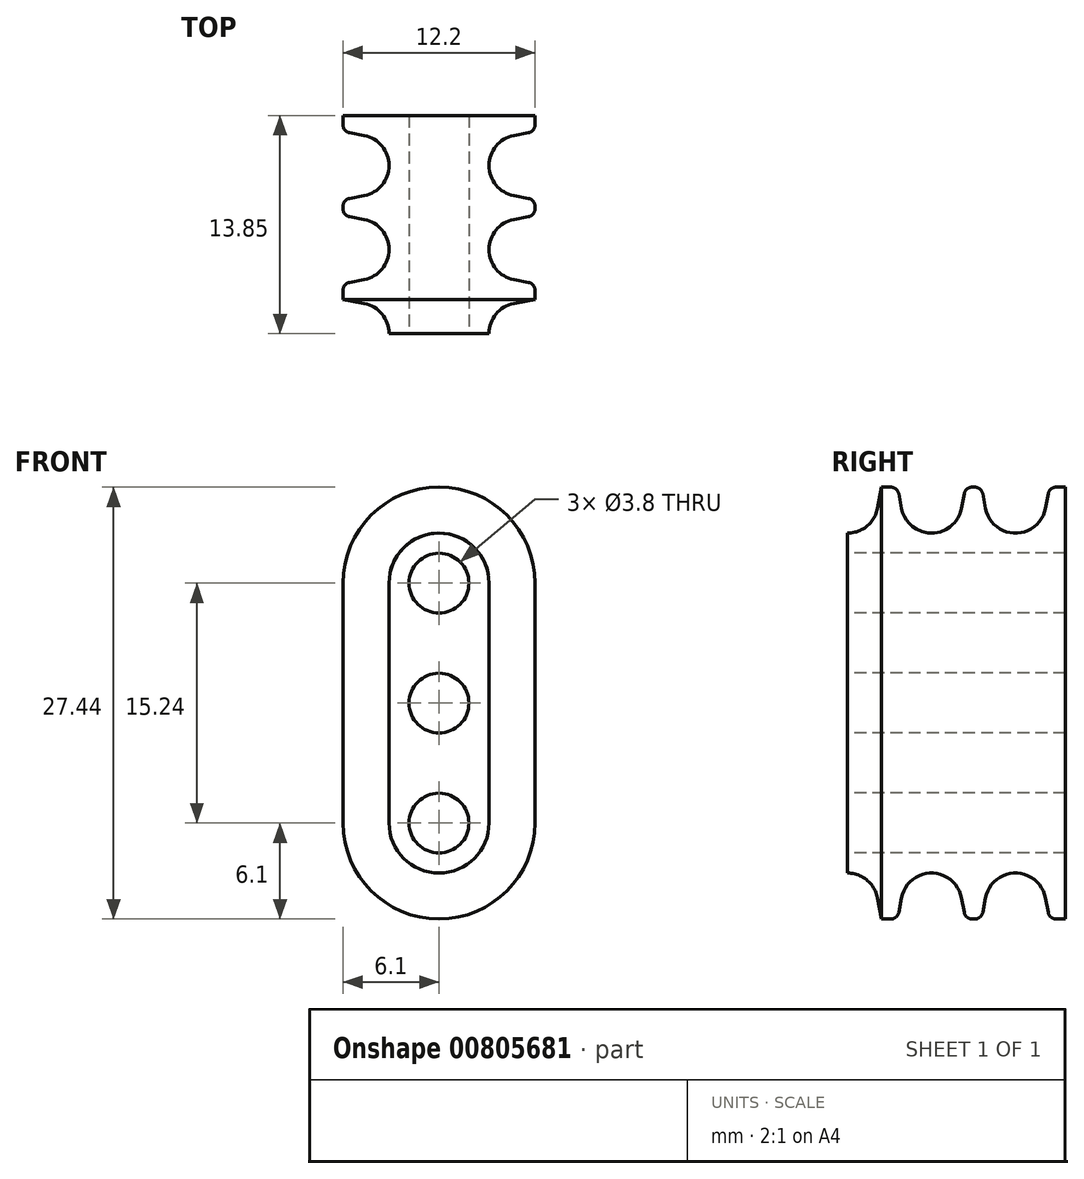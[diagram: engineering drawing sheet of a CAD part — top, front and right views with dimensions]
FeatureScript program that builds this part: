
annotation { "Feature Type Name" : "Feature", "Feature Type Description" : "" }
export const myFeature = defineFeature(function(context is Context, id is Id, definition is map)
    precondition{}
    {
        {
            var Q0;
            Q0=qCreatedBy(makeId("Front.planeOp"),FACE);
            var sketch = newSketch(context, id + "F0", { "sketchPlane" : qUnion([Q0])});
            skCircle(sketch, "E0", {"center": v(0, 0) * mm, "radius": 6.1 * mm});
            skSolve(sketch);
        }
        {
            var Q0;
            Q0=makeQuery(id+"F0.imprint","IMPRINT",FACE,{"disambiguationData":[TD([[makeQuery(id+"F0.imprint","IMPRINT",EDGE,{"derivedFrom":sQuery(id+"F0.wireOp",EDGE,"E0")}),1.0]])]});
            extrude(context, id + "F1", {"entities" : qUnion([Q0]), "depth" : 5.33 * mm, "offsetDistance" : 25.4 * mm, "symmetric" : true});
        }
        {
            var Q0;
            Q0=qCreatedBy(makeId("Front.planeOp"),FACE);
            var sketch = newSketch(context, id + "F2", { "sketchPlane" : qUnion([Q0])});
            skLineSegment(sketch, "E1.bottom", {"start": v(12.6, 0) * mm, "end": v(-13.53, 0) * mm});
            skLineSegment(sketch, "E1.top", {"start": v(12.6, -24.15) * mm, "end": v(-13.53, -24.15) * mm});
            skLineSegment(sketch, "E1.left", {"start": v(12.6, 0) * mm, "end": v(12.6, -24.15) * mm});
            skLineSegment(sketch, "E1.right", {"start": v(-13.53, 0) * mm, "end": v(-13.53, -24.15) * mm});
            skSolve(sketch);
        }
        {
            var Q0;
            Q0=qSketchRegion(id+"F2",true);
            extrude(context, id + "F3", {"entities" : qUnion([Q0]), "operationType" : NewBodyOperationType.REMOVE, "oppositeDirection" : true, "depth" : 25.4 * mm, "offsetDistance" : 25.4 * mm, "symmetric" : true});
        }
        {
            var Q0;
            Q0=makeQuery(id+"F1.opExtrude","CAP_FACE",FACE,{"disambiguationData":[OSD([sQuery(id+"F0.wireOp",EDGE,"E0")])],"isStart":false});
            var sketch = newSketch(context, id + "F4", { "sketchPlane" : qUnion([Q0])});
            skCircle(sketch, "E2", {"center": v(0, 0) * mm, "radius": 1.9 * mm});
            skSolve(sketch);
        }
        {
            var Q0;
            Q0=qCreatedBy(makeId("Right.planeOp"),FACE);
            var sketch = newSketch(context, id + "F5", { "sketchPlane" : qUnion([Q0])});
            skLineSegment(sketch, "E3", {"start": v(2.41, 7.44) * mm, "end": v(1.9, 4.75) * mm});
            skLineSegment(sketch, "E4", {"start": v(-2.41, 7.44) * mm, "end": v(-1.9, 4.75) * mm});
            skLineSegment(sketch, "E5", {"start": v(2.41, 7.44) * mm, "end": v(-2.41, 7.44) * mm});
            skArc(sketch, "E6", {"start": v(-1.9, 4.75) * mm, "mid": v(0, 3.17) * mm, "end": v(1.9, 4.75) * mm});
            skLineSegment(sketch, "E7", {"start": v(11.1, 0) * mm, "end": v(0, 0) * mm, "construction": true});
            skPoint(sketch, "E8", {"position": v(0, 3.18) * mm});
            skLineSegment(sketch, "E9", {"start": v(0, 0) * mm, "end": v(0, 5.11) * mm, "construction": true});
            skLineSegment(sketch, "E10.0", {"start": v(2.67, 0) * mm, "end": v(2.67, 6.1) * mm, "construction": true});
            skPoint(sketch, "E11", {"position": v(2.16, 6.1) * mm});
            skPoint(sketch, "E12", {"position": v(-2.16, 6.1) * mm});
            skLineSegment(sketch, "E13.direction1", {"start": v(-1.9, 4.75) * mm, "end": v(-7.24, 4.75) * mm, "construction": true});
            skLineSegment(sketch, "E14", {"start": v(2.16, 6.1) * mm, "end": v(2.67, 6.1) * mm, "construction": true});
            skLineSegment(sketch, "E15", {"start": v(-2.67, 6.1) * mm, "end": v(-2.16, 6.1) * mm, "construction": true});
            skSolve(sketch);
        }
        {
            var Q0;
            Q0=makeQuery(id+"F5.imprint","IMPRINT",FACE,{"disambiguationData":[TD([[makeQuery(id+"F5.imprint","IMPRINT",EDGE,{"derivedFrom":sQuery(id+"F5.wireOp",EDGE,"E3")}),-1.0]])]});
            var Q1;
            Q1=makeQuery(id+"F5.imprint","IMPRINT",FACE,{"disambiguationData":[TD([[makeQuery(id+"F5.imprint","IMPRINT",EDGE,{"derivedFrom":sQuery(id+"F5.wireOp",EDGE,"E13.1.0.0")}),-1.0]])]});
            var Q2;
            Q2=sQuery(id+"F5.wireOp",EDGE,"E7");
            var Q3;
            Q3=sQuery(id+"F5.wireOp",EDGE,"E7");
            revolve(context, id + "F6", {"operationType" : NewBodyOperationType.REMOVE, "surfaceOperationType" : NewSurfaceOperationType.NEW, "entities" : qUnion([Q0, Q1]), "surfaceEntities" : qUnion([Q2]), "axis" : qUnion([Q3]), "revolveType" : RevolveType.FULL, "oppositeDirection" : true});
        }
        {
            var Q0;
            {var subQ0=sQuery(id+"F2.wireOp",EDGE,"E1.bottom");Q0=makeQuery(id+"FzYgyNMxcEHEfbp_1.boolean.opBoolean","MERGE",FACE,{"derivedFrom":[makeQuery(id+"F3.boolean.opBoolean","COPY",FACE,{"derivedFrom":makeQuery(id+"F3.opExtrude","SWEPT_FACE",FACE,{"disambiguationData":[OSD([subQ0])]})}),makeQuery(id+"FzYgyNMxcEHEfbp_1.opExtrude","SWEPT_FACE",FACE,{"disambiguationData":[OSD([sQuery(id+"F0.wireOp",EDGE,"E0"),subQ0])]})]});}
            extrude(context, id + "F7", {"entities" : qUnion([Q0]), "operationType" : NewBodyOperationType.ADD, "depth" : 7.62 * mm, "offsetDistance" : 25.4 * mm});
        }
        {
            var Q0;
            Q0=makeQuery(id+"F1.opExtrude","SWEPT_BODY",BODY,{"disambiguationData":[OSD([sQuery(id+"F0.wireOp",EDGE,"E0")])]});
            var Q1;
            Q1=makeQuery(id+"F7.opExtrude","CAP_FACE",FACE,{"disambiguationData":[OSD([sQuery(id+"F0.wireOp",EDGE,"E0"),sQuery(id+"F2.wireOp",EDGE,"E1.bottom")])],"isStart":false});
            mirror(context, id + "F8", {"operationType" : NewBodyOperationType.ADD, "entities" : qUnion([Q0]), "mirrorPlane" : qUnion([Q1])});
        }
        {
            var Q0;
            Q0=makeQuery(id+"F1.opExtrude","SWEPT_BODY",BODY,{"disambiguationData":[OSD([sQuery(id+"F0.wireOp",EDGE,"E0")])]});
            var Q1;
            {var subQ0=sQuery(id+"F2.wireOp",EDGE,"E1.bottom");var subQ1=sQuery(id+"F0.wireOp",EDGE,"E0");var subQ2=makeQuery(id+"F1.opExtrude","CAP_FACE",FACE,{"disambiguationData":[OSD([subQ1])],"isStart":false});var subQ3=makeQuery(id+"F7.boolean.opBoolean","MERGE",FACE,{"derivedFrom":[subQ2,makeQuery(id+"F7.opExtrude","SWEPT_FACE",FACE,{"disambiguationData":[OSD([subQ1,subQ0]),TDD([makeQuery(id+"F3.boolean.opBoolean","INTERSECT",EDGE,{"derivedFrom":[subQ2,makeQuery(id+"F3.opExtrude","SWEPT_FACE",FACE,{"disambiguationData":[OSD([subQ0])]})]})])]})]});Q1=makeQuery(id+"F8.boolean.opBoolean","MERGE",FACE,{"derivedFrom":[subQ3,makeQuery(id+"F8.opPattern","COPY",FACE,{"derivedFrom":subQ3,"instanceName":"1"})]});}
            mirror(context, id + "F9", {"operationType" : NewBodyOperationType.ADD, "entities" : qUnion([Q0]), "mirrorPlane" : qUnion([Q1])});
        }
        {
            var Q0;
            Q0=qCreatedBy(makeId("Right.planeOp"),FACE);
            var sketch = newSketch(context, id + "F10", { "sketchPlane" : qUnion([Q0])});
            skLineSegment(sketch, "E16.bottom", {"start": v(-5.33, 7.62) * mm, "end": v(-15.12, 7.62) * mm});
            skLineSegment(sketch, "E16.top", {"start": v(-5.33, -23.05) * mm, "end": v(-15.12, -23.05) * mm});
            skLineSegment(sketch, "E16.left", {"start": v(-5.33, 7.62) * mm, "end": v(-5.33, -23.05) * mm});
            skLineSegment(sketch, "E16.right", {"start": v(-15.12, 7.62) * mm, "end": v(-15.12, -23.05) * mm});
            skSolve(sketch);
        }
        {
            var Q0;
            Q0 = qSketchRegion(id + "F10", true);
            extrude(context, id + "F11", {"entities" : qUnion([Q0]), "operationType" : NewBodyOperationType.REMOVE, "oppositeDirection" : true, "depth" : 25.4 * mm, "offsetDistance" : 25.4 * mm, "symmetric" : true});
        }
        {
            var Q0;
            Q0=makeQuery(id+"F1.opExtrude","SWEPT_BODY",BODY,{"disambiguationData":[OSD([sQuery(id+"F0.wireOp",EDGE,"E0")])]});
            var Q1;
            Q1=makeQuery(id+"F11.boolean.opBoolean","COPY",FACE,{"derivedFrom":makeQuery(id+"F11.opExtrude","SWEPT_FACE",FACE,{"disambiguationData":[OSD([sQuery(id+"F10.wireOp",EDGE,"E16.left")])]})});
            mirror(context, id + "F12", {"operationType" : NewBodyOperationType.ADD, "entities" : qUnion([Q0]), "mirrorPlane" : qUnion([Q1])});
        }
        {
            var Q0;
            Q0=qSketchRegion(id+"F4",true);
            extrude(context, id + "F13", {"entities" : qUnion([Q0]), "operationType" : NewBodyOperationType.REMOVE, "oppositeDirection" : true, "depth" : 127 * mm, "offsetDistance" : 25.4 * mm, "symmetric" : true});
        }
        {
            var Q0;
            {var subQ0=sQuery(id+"F2.wireOp",EDGE,"E1.bottom");var subQ1=sQuery(id+"F0.wireOp",EDGE,"E0");var subQ2=makeQuery(id+"F1.opExtrude","CAP_FACE",FACE,{"disambiguationData":[OSD([subQ1])],"isStart":true});var subQ3=makeQuery(id+"F7.boolean.opBoolean","MERGE",FACE,{"derivedFrom":[subQ2,makeQuery(id+"F7.opExtrude","SWEPT_FACE",FACE,{"disambiguationData":[OSD([subQ1,subQ0]),TDD([makeQuery(id+"F3.boolean.opBoolean","INTERSECT",EDGE,{"derivedFrom":[subQ2,makeQuery(id+"F3.opExtrude","SWEPT_FACE",FACE,{"disambiguationData":[OSD([subQ0])]})]})])]})]});Q0=makeQuery(id+"F8.boolean.opBoolean","MERGE",FACE,{"derivedFrom":[subQ3,makeQuery(id+"F8.opPattern","COPY",FACE,{"derivedFrom":subQ3,"instanceName":"1"})]});}
            extrude(context, id + "F14", {"entities" : qUnion([Q0]), "operationType" : NewBodyOperationType.ADD, "depth" : 0.5 * mm, "offsetDistance" : 25.4 * mm});
        }
        {
            var Q0;
            Q0=qCreatedBy(makeId("Front.planeOp"),FACE);
            var sketch = newSketch(context, id + "F15", { "sketchPlane" : qUnion([Q0])});
            skCircle(sketch, "E17.0", {"center": v(0, 0) * mm, "radius": 1.9 * mm});
            skCircle(sketch, "E18.0.1.0", {"center": v(0, -7.62) * mm, "radius": 1.9 * mm});
            skCircle(sketch, "E18.0.2.0", {"center": v(0, -15.24) * mm, "radius": 1.9 * mm});
            skLineSegment(sketch, "E18.direction1", {"start": v(0, 0) * mm, "end": v(25.4, 0) * mm, "construction": true});
            skLineSegment(sketch, "E18.direction2", {"start": v(0, 0) * mm, "end": v(0, -7.62) * mm, "construction": true});
            skSolve(sketch);
        }
        {
            var Q0;
            Q0 = qSketchRegion(id + "F15", true);
            var Q1;
            Q1=sQuery(id+"F15.wireOp",EDGE,"E18.0.1.0");
            var Q2;
            Q2=sQuery(id+"F15.wireOp",EDGE,"E18.0.2.0");
            extrude(context, id + "F16", {"entities" : qUnion([Q0]), "operationType" : NewBodyOperationType.REMOVE, "surfaceEntities" : qUnion([Q1, Q2]), "oppositeDirection" : true, "depth" : 127 * mm, "offsetDistance" : 25.4 * mm, "symmetric" : true});
        }
        {
            var Q0;
            {var subQ0=sQuery(id+"F0.wireOp",EDGE,"E0");Q0=makeQuery(id+"F6.boolean.opBoolean","INTERSECT",EDGE,{"derivedFrom":[makeQuery(id+"FzYgyNMxcEHEfbp_1.boolean.opBoolean","MERGE",FACE,{"derivedFrom":[makeQuery(id+"F1.opExtrude","SWEPT_FACE",FACE,{"disambiguationData":[OSD([subQ0])]}),makeQuery(id+"FzYgyNMxcEHEfbp_1.opExtrude","SWEPT_FACE",FACE,{"disambiguationData":[OSD([subQ0])]})]}),makeQuery(id+"F6.opRevolve","SWEPT_FACE",FACE,{"disambiguationData":[OSD([sQuery(id+"F5.wireOp",EDGE,"E4")])]})]});}
            var Q1;
            {var subQ0=sQuery(id+"F0.wireOp",EDGE,"E0");Q1=makeQuery(id+"F6.boolean.opBoolean","INTERSECT",EDGE,{"derivedFrom":[makeQuery(id+"FzYgyNMxcEHEfbp_1.boolean.opBoolean","MERGE",FACE,{"derivedFrom":[makeQuery(id+"F1.opExtrude","SWEPT_FACE",FACE,{"disambiguationData":[OSD([subQ0])]}),makeQuery(id+"FzYgyNMxcEHEfbp_1.opExtrude","SWEPT_FACE",FACE,{"disambiguationData":[OSD([subQ0])]})]}),makeQuery(id+"F6.opRevolve","SWEPT_FACE",FACE,{"disambiguationData":[OSD([sQuery(id+"F5.wireOp",EDGE,"E3")])]})]});}
            var Q2;
            Q2=makeQuery(id+"F9.opPattern","COPY",EDGE,{"derivedFrom":makeQuery(id+"F6.boolean.opBoolean","INTERSECT",EDGE,{"derivedFrom":[makeQuery(id+"F1.opExtrude","SWEPT_FACE",FACE,{"disambiguationData":[OSD([sQuery(id+"F0.wireOp",EDGE,"E0")])]}),makeQuery(id+"F6.opRevolve","SWEPT_FACE",FACE,{"disambiguationData":[OSD([sQuery(id+"F5.wireOp",EDGE,"E4")])]})]}),"instanceName":"1"});
            var Q3;
            Q3=makeQuery(id+"F12.opPattern","COPY",EDGE,{"derivedFrom":makeQuery(id+"F9.opPattern","COPY",EDGE,{"derivedFrom":makeQuery(id+"F6.boolean.opBoolean","INTERSECT",EDGE,{"derivedFrom":[makeQuery(id+"F1.opExtrude","SWEPT_FACE",FACE,{"disambiguationData":[OSD([sQuery(id+"F0.wireOp",EDGE,"E0")])]}),makeQuery(id+"F6.opRevolve","SWEPT_FACE",FACE,{"disambiguationData":[OSD([sQuery(id+"F5.wireOp",EDGE,"E4")])]})]}),"instanceName":"1"}),"instanceName":"1"});
            fillet(context, id + "F17", {"entities" : qUnion([Q0, Q1, Q2, Q3]), "radius" : 0.5 * mm, "tangentPropagation" : true, "allowEdgeOverflow" : false});
        }
        {
            var Q0;
            Q0=qCreatedBy(makeId("Right.planeOp"),FACE);
            var sketch = newSketch(context, id + "F18", { "sketchPlane" : qUnion([Q0])});
            skLineSegment(sketch, "E19.bottom", {"start": v(-18.16, 9.74) * mm, "end": v(-10.67, 9.74) * mm});
            skLineSegment(sketch, "E19.top", {"start": v(-18.16, -24.18) * mm, "end": v(-10.67, -24.18) * mm});
            skLineSegment(sketch, "E19.left", {"start": v(-18.16, 9.74) * mm, "end": v(-18.16, -24.18) * mm});
            skLineSegment(sketch, "E19.right", {"start": v(-10.67, 9.74) * mm, "end": v(-10.67, -24.18) * mm});
            skSolve(sketch);
        }
        {
            var Q0;
            Q0 = qSketchRegion(id + "F18", true);
            extrude(context, id + "F19", {"entities" : qUnion([Q0]), "operationType" : NewBodyOperationType.REMOVE, "depth" : 25.4 * mm, "offsetDistance" : 25.4 * mm, "symmetric" : true});
        }
    });
